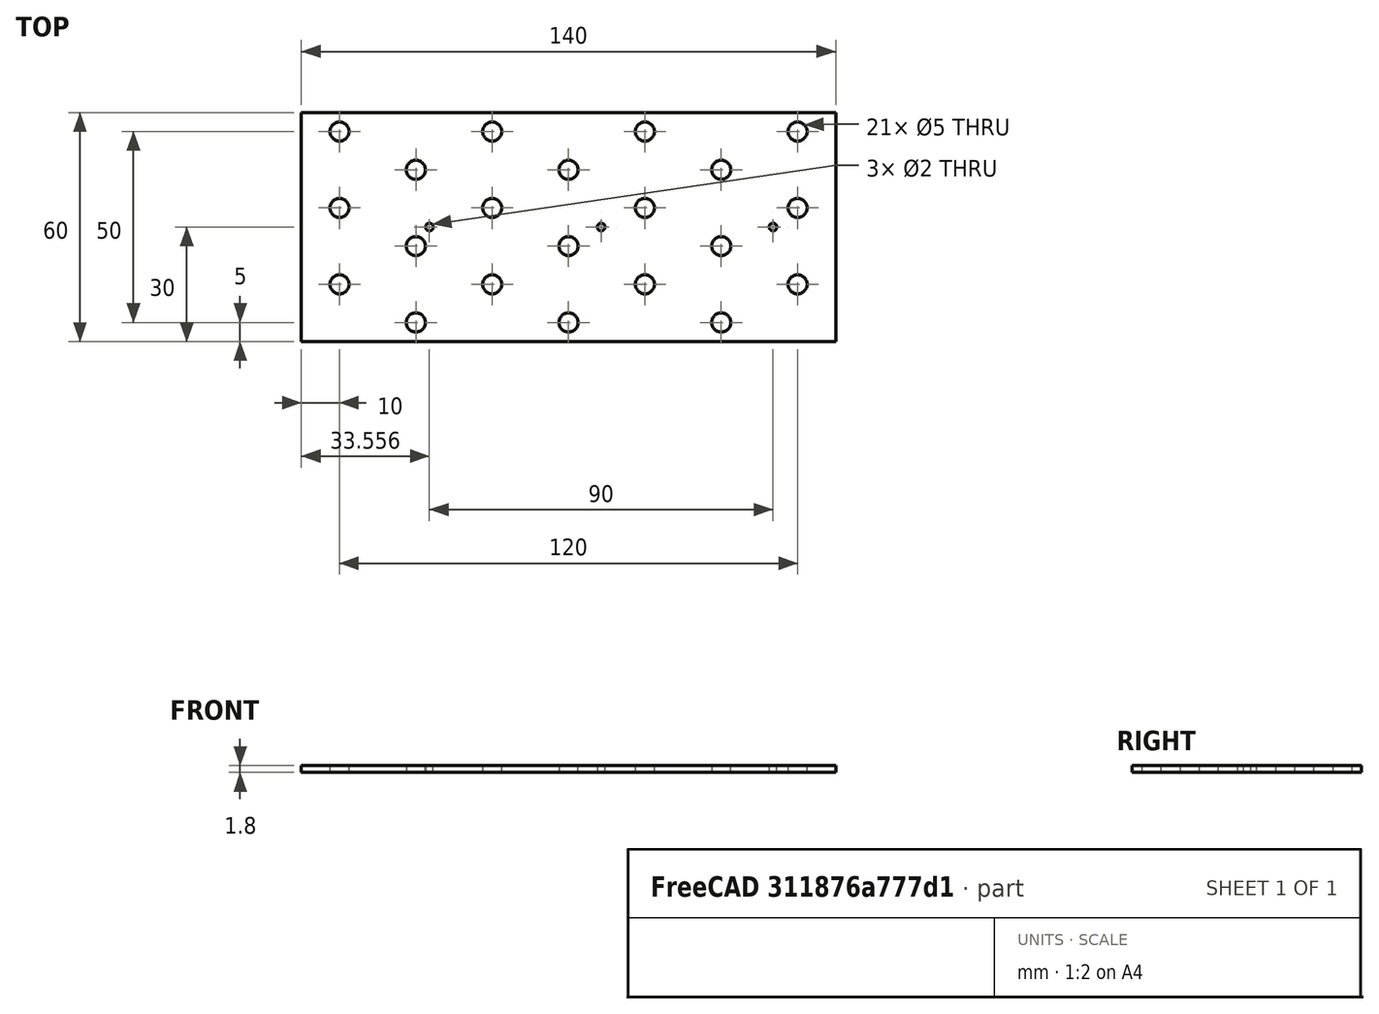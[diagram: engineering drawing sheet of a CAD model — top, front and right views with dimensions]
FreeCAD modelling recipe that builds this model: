
FCSTD DOCUMENT  (FreeCAD 0.19R24276 (Git))
Label: Bar_60x140__1_8mm
License: All rights reserved
LicenseURL: http://en.wikipedia.org/wiki/All_rights_reserved
objects: Sketcher::SketchObject×1, PartDesign::Pad×1, PartDesign::Body×1
note: 4 computed .brp shape members not serialized (recipe doc carries the construction recipe); baked Part::Feature solids carry a one-line shape summary decoded from their .brp

FEATURE [Sketcher::SketchObject] Sketch
  FullyConstrained = false
  MapMode = 5
  Support = -> [XY_Plane]
  sketch-geometry (52):
    g0: LineSegment StartX=0 StartY=0 StartZ=0 EndX=120 EndY=0 EndZ=0
    g1: LineSegment StartX=120 StartY=0 StartZ=0 EndX=120 EndY=80 EndZ=0
    g2: LineSegment StartX=120 StartY=80 StartZ=0 EndX=0 EndY=80 EndZ=0
    g3: LineSegment StartX=0 StartY=80 StartZ=0 EndX=0 EndY=0 EndZ=0
    g4: LineSegment StartX=0 StartY=4.5 StartZ=0 EndX=120 EndY=4.5 EndZ=0
    g5: LineSegment StartX=0 StartY=24.5 StartZ=0 EndX=120 EndY=24.5 EndZ=0
    g6: LineSegment StartX=0 StartY=44.5 StartZ=0 EndX=120 EndY=44.5 EndZ=0
    g7: LineSegment StartX=0 StartY=64.5 StartZ=0 EndX=120 EndY=64.5 EndZ=0
    g8: LineSegment StartX=48.5 StartY=0 StartZ=0 EndX=48.5 EndY=4.5 EndZ=0
    g9: LineSegment StartX=68.5 StartY=0 StartZ=0 EndX=68.5 EndY=4.5 EndZ=0
    g10: LineSegment StartX=88.5 StartY=0 StartZ=0 EndX=88.5 EndY=4.5 EndZ=0
    g11: LineSegment StartX=108.5 StartY=0 StartZ=0 EndX=108.5 EndY=4.5 EndZ=0
    g12: LineSegment StartX=0 StartY=14.5 StartZ=0 EndX=120 EndY=14.5 EndZ=0
    g13: LineSegment StartX=0 StartY=34.5 StartZ=0 EndX=120 EndY=34.5 EndZ=0
    g14: LineSegment StartX=0 StartY=54.5 StartZ=0 EndX=120 EndY=54.5 EndZ=0
    g15: LineSegment StartX=0 StartY=74.5 StartZ=0 EndX=120 EndY=74.5 EndZ=0
    g16: LineSegment StartX=48.5 StartY=24.5 StartZ=0 EndX=48.5 EndY=80 EndZ=0
    g17: LineSegment StartX=68.5 StartY=14.5 StartZ=0 EndX=68.5 EndY=80 EndZ=0
    g18: LineSegment StartX=88.5 StartY=24.5 StartZ=0 EndX=88.5 EndY=80 EndZ=0
    g19: LineSegment StartX=108.5 StartY=14.5 StartZ=0 EndX=108.5 EndY=80 EndZ=0
    g20: Circle CenterX=28.5 CenterY=14.5 CenterZ=0 NormalX=0 NormalY=0 NormalZ=1 AngleXU=0 Radius=2.5
    g21: Circle CenterX=108.5 CenterY=14.5 CenterZ=0 NormalX=0 NormalY=0 NormalZ=1 AngleXU=0 Radius=2.5
    g22: Circle CenterX=8.5 CenterY=24.5 CenterZ=0 NormalX=0 NormalY=0 NormalZ=1 AngleXU=0 Radius=2.5
    g23: Circle CenterX=48.5 CenterY=24.5 CenterZ=0 NormalX=0 NormalY=0 NormalZ=1 AngleXU=0 Radius=2.5
    g24: Circle CenterX=88.5 CenterY=24.5 CenterZ=0 NormalX=0 NormalY=0 NormalZ=1 AngleXU=0 Radius=2.5
    g25: Circle CenterX=8.5 CenterY=44.5 CenterZ=0 NormalX=0 NormalY=0 NormalZ=1 AngleXU=0 Radius=2.5
    g26: Circle CenterX=48.5 CenterY=44.5 CenterZ=0 NormalX=0 NormalY=0 NormalZ=1 AngleXU=0 Radius=2.5
    g27: Circle CenterX=88.5 CenterY=44.5 CenterZ=0 NormalX=0 NormalY=0 NormalZ=1 AngleXU=0 Radius=2.5
    g28: Circle CenterX=28.5 CenterY=54.5 CenterZ=0 NormalX=0 NormalY=0 NormalZ=1 AngleXU=0 Radius=2.5
    g29: Circle CenterX=68.5 CenterY=54.5 CenterZ=0 NormalX=0 NormalY=0 NormalZ=1 AngleXU=0 Radius=2.5
    g30: Circle CenterX=108.5 CenterY=54.5 CenterZ=0 NormalX=0 NormalY=0 NormalZ=1 AngleXU=0 Radius=2.5
    g31: Circle CenterX=88.5 CenterY=64.5 CenterZ=0 NormalX=0 NormalY=0 NormalZ=1 AngleXU=0 Radius=2.5
    g32: Circle CenterX=48.5 CenterY=64.5 CenterZ=0 NormalX=0 NormalY=0 NormalZ=1 AngleXU=0 Radius=2.5
    g33: Circle CenterX=8.5 CenterY=64.5 CenterZ=0 NormalX=0 NormalY=0 NormalZ=1 AngleXU=0 Radius=2.5
    g34: Circle CenterX=28.5 CenterY=34.5 CenterZ=0 NormalX=0 NormalY=0 NormalZ=1 AngleXU=0 Radius=2.5
    g35: Circle CenterX=68.5 CenterY=34.5 CenterZ=0 NormalX=0 NormalY=0 NormalZ=1 AngleXU=0 Radius=2.5
    g36: Circle CenterX=108.5 CenterY=34.5 CenterZ=0 NormalX=0 NormalY=0 NormalZ=1 AngleXU=0 Radius=2.5
    g37: LineSegment StartX=28.5 StartY=74.5 StartZ=0 EndX=28.5 EndY=14.5 EndZ=0
    g38: LineSegment StartX=8.5 StartY=4.5 StartZ=0 EndX=8.5 EndY=24.5 EndZ=0
    g39: Circle CenterX=68.5 CenterY=14.5 CenterZ=0 NormalX=0 NormalY=0 NormalZ=1 AngleXU=0 Radius=2.5
    g40: LineSegment StartX=-1.5 StartY=9.5 StartZ=0 EndX=138.5 EndY=9.5 EndZ=0
    g41: LineSegment StartX=-1.5 StartY=69.5 StartZ=0 EndX=138.5 EndY=69.5 EndZ=0
    g42: LineSegment StartX=-1.5 StartY=69.5 StartZ=0 EndX=-1.5 EndY=9.5 EndZ=0
    g43: LineSegment StartX=138.5 StartY=69.5 StartZ=0 EndX=138.5 EndY=9.5 EndZ=0
    g44: Circle CenterX=128.5 CenterY=24.5 CenterZ=0 NormalX=0 NormalY=0 NormalZ=1 AngleXU=0 Radius=2.5
    g45: Circle CenterX=128.5 CenterY=44.5 CenterZ=0 NormalX=0 NormalY=0 NormalZ=1 AngleXU=0 Radius=2.5
    g46: Circle CenterX=128.5 CenterY=64.5 CenterZ=0 NormalX=0 NormalY=0 NormalZ=1 AngleXU=0 Radius=2.5
    g47: Circle CenterX=77.056 CenterY=39.5 CenterZ=0 NormalX=0 NormalY=0 NormalZ=1 AngleXU=0 Radius=1
    g48: LineSegment StartX=77.056 StartY=39.5 StartZ=0 EndX=122.056 EndY=39.5 EndZ=0
    g49: Circle CenterX=122.056 CenterY=39.5 CenterZ=0 NormalX=0 NormalY=0 NormalZ=1 AngleXU=0 Radius=1
    g50: LineSegment StartX=77.056 StartY=39.5 StartZ=0 EndX=77.056 EndY=52.3412 EndZ=0
    g51: Circle CenterX=32.056 CenterY=39.5 CenterZ=0 NormalX=0 NormalY=0 NormalZ=1 AngleXU=0 Radius=1
  constraints (109):
    c: Coincident(g0,g1)
    c: Coincident(g1,g2)
    c: Coincident(g2,g3)
    c: Coincident(g3,g0)
    c: Horizontal(g0)
    c: Horizontal(g2)
    c: Vertical(g1)
    c: Vertical(g3)
    c: Coincident(g0,g-1)
    c: DistanceX(g0,g0) = 120
    c: DistanceY(g3,g3) = 80
    c: Horizontal(g4)
    c: PointOnObject(g4,g3)
    c: PointOnObject(g4,g1)
    c: Horizontal(g5)
    c: PointOnObject(g5,g3)
    c: PointOnObject(g5,g1)
    c: DistanceY(g4,g5) = 20
    c: Horizontal(g6)
    c: PointOnObject(g6,g1)
    c: PointOnObject(g6,g3)
    c: DistanceY(g5,g6) = 20
    c: Horizontal(g7)
    c: PointOnObject(g7,g1)
    c: PointOnObject(g7,g3)
    c: DistanceY(g6,g7) = 20
    c: Vertical(g8)
    c: Vertical(g9)
    c: Vertical(g10)
    c: Vertical(g11)
    c: PointOnObject(g8,g0)
    c: PointOnObject(g9,g0)
    c: PointOnObject(g10,g0)
    c: PointOnObject(g11,g0)
    c: PointOnObject(g19,g2)
    c: PointOnObject(g18,g2)
    c: PointOnObject(g17,g2)
    c: PointOnObject(g16,g2)
    c: DistanceX(g8,g9) = 20
    c: DistanceX(g9,g10) = 20
    c: DistanceX(g10,g11) = 20
    c: Horizontal(g12)
    c: Horizontal(g13)
    c: Horizontal(g14)
    c: Horizontal(g15)
    c: PointOnObject(g12,g3)
    c: PointOnObject(g13,g3)
    c: PointOnObject(g14,g3)
    c: PointOnObject(g15,g3)
    c: PointOnObject(g15,g1)
    c: PointOnObject(g14,g1)
    c: PointOnObject(g13,g1)
    c: PointOnObject(g12,g1)
    c: DistanceY(g0,g12) = 14.5
    c: DistanceY(g12,g13) = 20
    c: DistanceY(g13,g14) = 20
    c: DistanceY(g14,g15) = 20
    c: PointOnObject(g20,g12)
    c: PointOnObject(g8,g4)
    c: Tangent(g8,g16)
    c: PointOnObject(g9,g4)
    c: PointOnObject(g17,g12)
    c: Tangent(g9,g17)
    c: PointOnObject(g10,g4)
    c: Tangent(g10,g18)
    c: PointOnObject(g11,g4)
    c: PointOnObject(g19,g12)
    c: Tangent(g11,g19)
    c: Coincident(g21,g19)
    c: Diameter(g20) = 5
    c: PointOnObject(g16,g5)
    c: PointOnObject(g18,g5)
    c: Equal(g23,g24)
    c: Equal(g33,g28)
    c: Equal(g28,g32)
    c: Equal(g32,g31)
    c: Equal(g31,g30)
    c: Diameter(g28) = 5
    c: Equal(g31,g29)
    c: Equal(g26,g27)
    c: Diameter(g34) = 5
    c: Coincident(g37,g20)
    c: Vertical(g37)
    c: DistanceY(g0,g4) = 4.5
    c: Coincident(g38,g22)
    c: Vertical(g38)
    c: Coincident(g39,g17)
    c: Equal(g21,g39)
    c: Horizontal(g40)
    c: Horizontal(g41)
    c: Vertical(g42)
    c: DistanceX(g0,g38) = 8.5
    c: Coincident(g42,g40)
    c: Coincident(g41,g42)
    c: Vertical(g43)
    c: DistanceX(g40,g38) = 10
    c: Coincident(g40,g43)
    c: DistanceY(g40,g21) = 5
    c: Coincident(g41,g43)
    c: DistanceY(g40,g41) = 60
    c: DistanceX(g41,g41) = 140
    c: Diameter(g47) = 2
    c: Coincident(g48,g47)
    c: Horizontal(g48)
    c: Coincident(g49,g48)
    c: Equal(g49,g47)
    c: DistanceX(g48,g48) = 45
    c: Coincident(g50,g47)
    c: Vertical(g50)
FEATURE [PartDesign::Pad] Pad
  Direction = (1,1,1)
  Length = 1.8
  Length2 = 100
  Profile = -> Sketch
  Type = 0
FEATURE [PartDesign::Body] Body
  Group = -> [Sketch,Pad]
  Origin = -> Origin
  Tip = -> Pad
